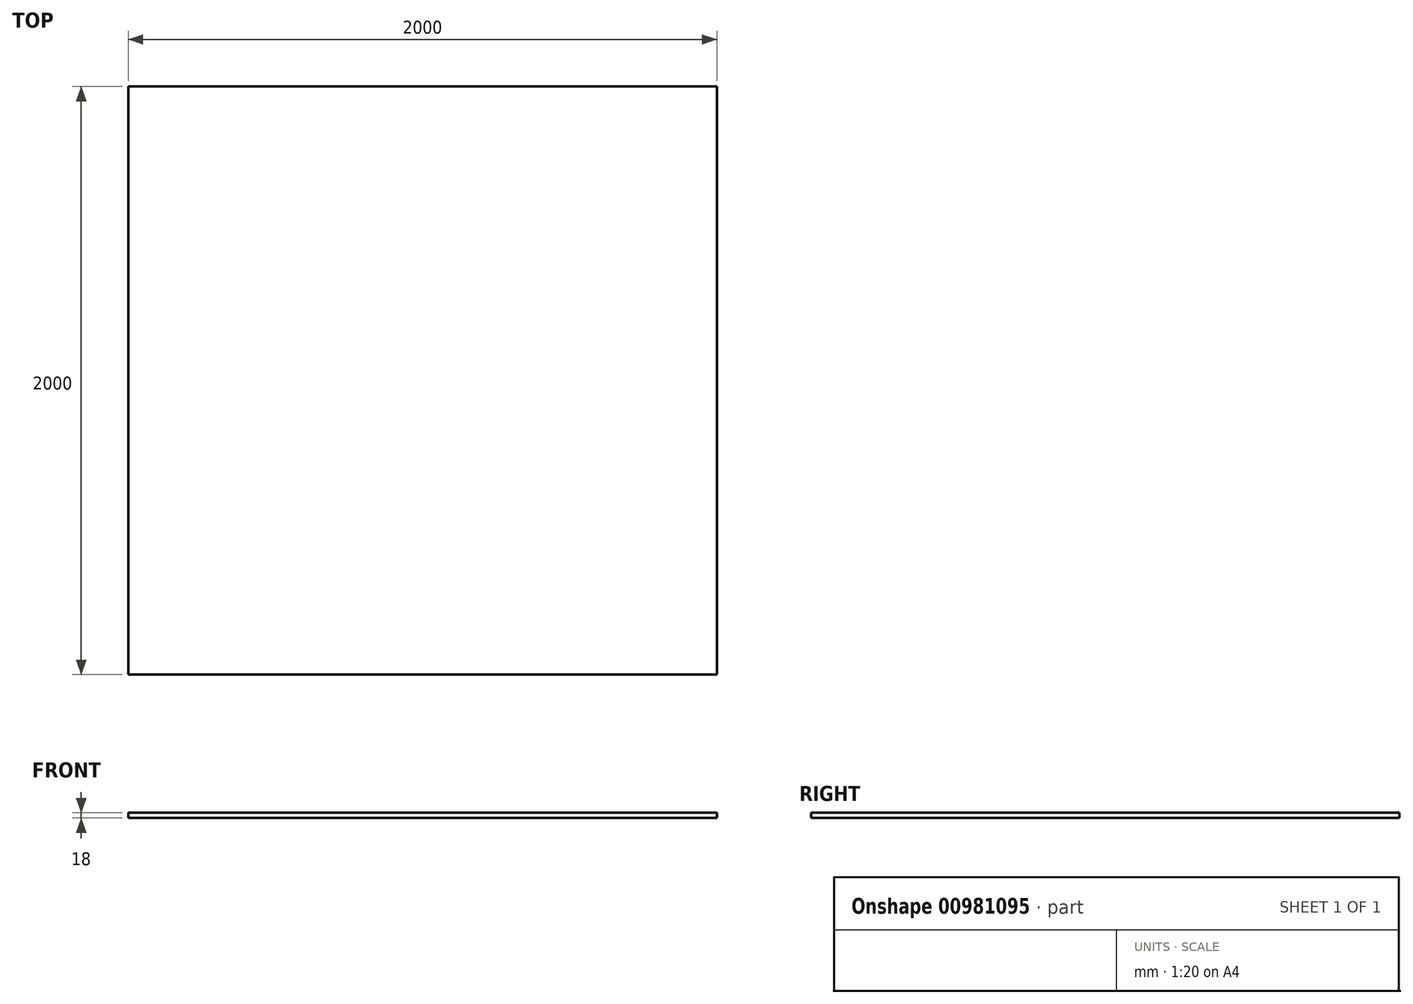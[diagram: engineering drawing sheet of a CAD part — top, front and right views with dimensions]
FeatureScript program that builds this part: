
annotation { "Feature Type Name" : "Feature", "Feature Type Description" : "" }
export const myFeature = defineFeature(function(context is Context, id is Id, definition is map)
    precondition{}
    {
        {
            var Q0;
            Q0=qCreatedBy(makeId("Top.planeOp"),FACE);
            var sketch = newSketch(context, id + "F0", { "sketchPlane" : qUnion([Q0])});
            skLineSegment(sketch, "E0.bottom", {"start": v(-986.01, 996.32) * mm, "end": v(1013.99, 996.32) * mm});
            skLineSegment(sketch, "E0.top", {"start": v(-986.01, -1003.68) * mm, "end": v(1013.99, -1003.68) * mm});
            skLineSegment(sketch, "E0.left", {"start": v(-986.01, 996.32) * mm, "end": v(-986.01, -1003.68) * mm});
            skLineSegment(sketch, "E0.right", {"start": v(1013.99, 996.32) * mm, "end": v(1013.99, -1003.68) * mm});
            skSolve(sketch);
        }
        {
            var Q0;
            Q0 = qSketchRegion(id + "F0", true);
            extrude(context, id + "F1", {"entities" : qUnion([Q0]), "depth" : 18 * mm, "offsetDistance" : 25.4 * mm});
        }
    });
